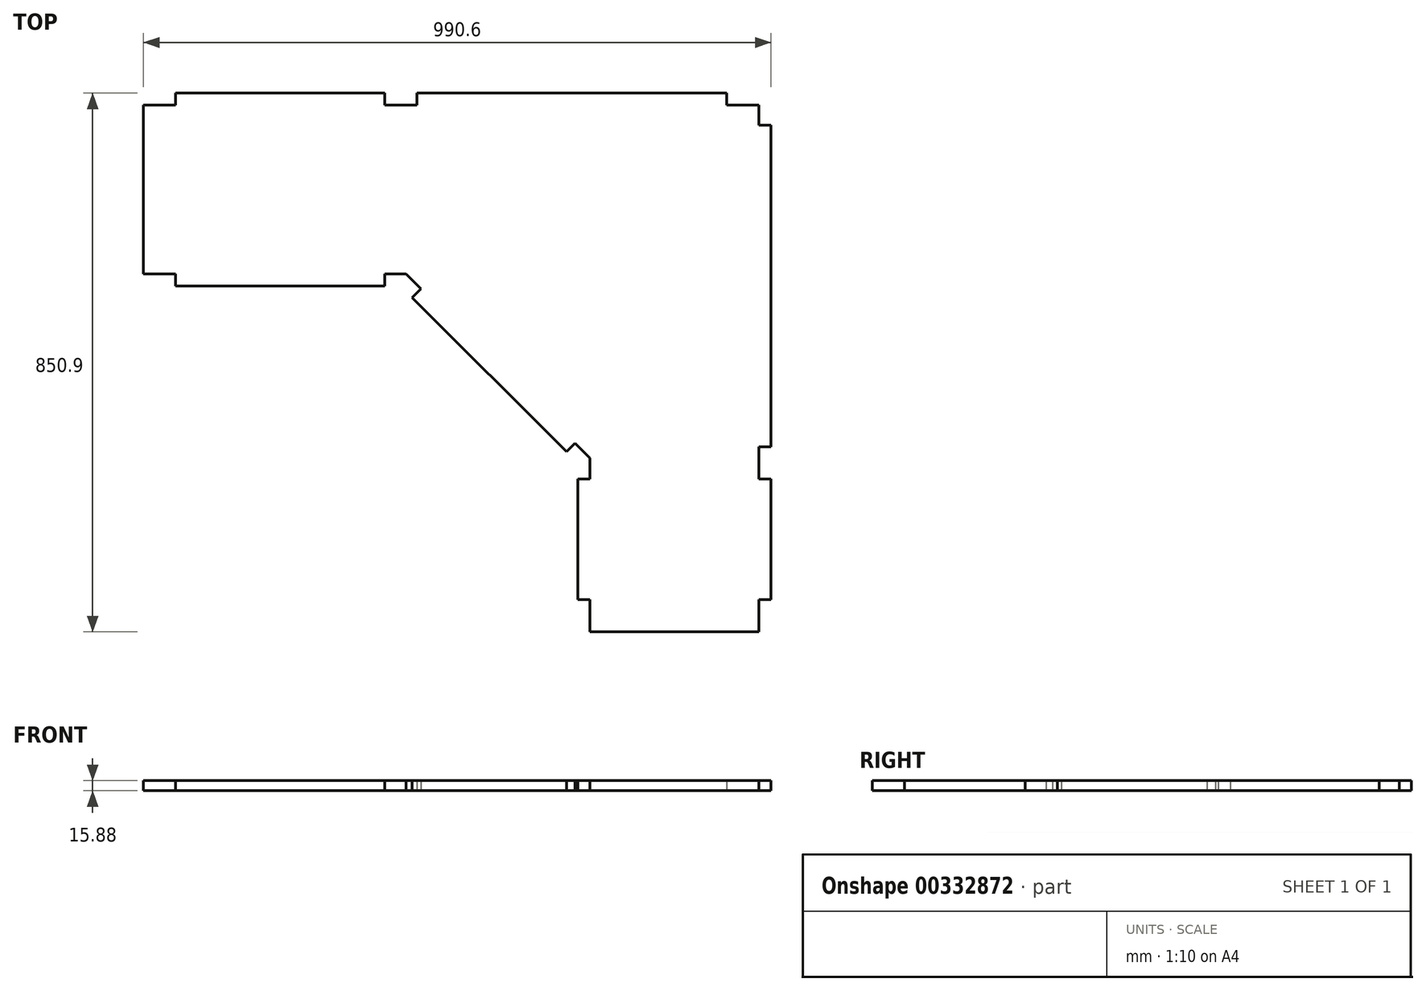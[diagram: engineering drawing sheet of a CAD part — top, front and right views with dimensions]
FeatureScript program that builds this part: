
annotation { "Feature Type Name" : "Feature", "Feature Type Description" : "" }
export const myFeature = defineFeature(function(context is Context, id is Id, definition is map)
    precondition{}
    {
        {
            var Q0;
            Q0=qCreatedBy(makeId("Top.planeOp"),FACE);
            var sketch = newSketch(context, id + "F0", { "sketchPlane" : qUnion([Q0])});
            skLineSegment(sketch, "E0.bottom", {"start": v(209.55, -425.45) * mm, "end": v(476.25, -425.45) * mm});
            skLineSegment(sketch, "E0.top", {"start": v(-444.5, 425.45) * mm, "end": v(-114.41, 425.45) * mm});
            skLineSegment(sketch, "E0.left", {"start": v(-495.3, 139.7) * mm, "end": v(-495.3, 406.4) * mm});
            skLineSegment(sketch, "E0.right", {"start": v(495.3, -374.65) * mm, "end": v(495.3, -184.26) * mm});
            skPoint(sketch, "E0.middle", {"position": v(0, 0) * mm});
            skLineSegment(sketch, "E1.left", {"start": v(190.5, -374.65) * mm, "end": v(190.5, -184.26) * mm});
            skPoint(sketch, "E2.orphan", {"position": v(-495.3, -425.45) * mm});
            skLineSegment(sketch, "E3", {"start": v(172.54, -140.9) * mm, "end": v(-71.05, 102.69) * mm});
            skLineSegment(sketch, "E4", {"start": v(-444.5, 120.65) * mm, "end": v(-114.41, 120.65) * mm});
            skLineSegment(sketch, "E5.top", {"start": v(-495.3, 139.7) * mm, "end": v(-444.5, 139.7) * mm});
            skLineSegment(sketch, "E5.right", {"start": v(-444.5, 120.65) * mm, "end": v(-444.5, 139.7) * mm});
            skLineSegment(sketch, "E6.top", {"start": v(-495.3, 406.4) * mm, "end": v(-444.5, 406.4) * mm});
            skLineSegment(sketch, "E6.right", {"start": v(-444.5, 425.45) * mm, "end": v(-444.5, 406.4) * mm});
            skLineSegment(sketch, "E7.top", {"start": v(190.5, -374.65) * mm, "end": v(209.55, -374.65) * mm});
            skLineSegment(sketch, "E7.right", {"start": v(209.55, -425.45) * mm, "end": v(209.55, -374.65) * mm});
            skLineSegment(sketch, "E8.top", {"start": v(476.25, -374.65) * mm, "end": v(495.3, -374.65) * mm});
            skLineSegment(sketch, "E8.left", {"start": v(476.25, -425.45) * mm, "end": v(476.25, -374.65) * mm});
            skPoint(sketch, "E9.orphan", {"position": v(-495.3, 425.45) * mm});
            skPoint(sketch, "E10.orphan", {"position": v(495.3, -425.45) * mm});
            skLineSegment(sketch, "E11.top", {"start": v(476.25, 406.4) * mm, "end": v(425.45, 406.4) * mm});
            skLineSegment(sketch, "E11.right", {"start": v(425.45, 425.45) * mm, "end": v(425.45, 406.4) * mm});
            skLineSegment(sketch, "E12.bottom", {"start": v(476.25, 374.65) * mm, "end": v(495.3, 374.65) * mm});
            skLineSegment(sketch, "E12.left", {"start": v(476.25, 374.65) * mm, "end": v(476.25, 406.4) * mm});
            skPoint(sketch, "E13.orphan", {"position": v(495.3, 425.45) * mm});
            skLineSegment(sketch, "E14.top", {"start": v(-114.41, 139.7) * mm, "end": v(-81.12, 139.7) * mm});
            skLineSegment(sketch, "E14.left", {"start": v(-114.41, 120.65) * mm, "end": v(-114.41, 139.7) * mm});
            skLineSegment(sketch, "E15.bottom", {"start": v(190.5, -184.26) * mm, "end": v(209.55, -184.26) * mm});
            skLineSegment(sketch, "E15.right", {"start": v(209.55, -184.26) * mm, "end": v(209.55, -150.97) * mm});
            skLineSegment(sketch, "E16", {"start": v(-81.12, 139.7) * mm, "end": v(-57.58, 116.16) * mm});
            skLineSegment(sketch, "E17", {"start": v(172.54, -140.9) * mm, "end": v(186, -127.43) * mm});
            skPoint(sketch, "E18.orphan", {"position": v(190.5, -158.86) * mm});
            skLineSegment(sketch, "E19", {"start": v(-71.05, 102.69) * mm, "end": v(-57.58, 116.16) * mm});
            skPoint(sketch, "E20.orphan", {"position": v(-89.01, 120.65) * mm});
            skLineSegment(sketch, "E21.trimOffspring", {"start": v(186, -127.43) * mm, "end": v(209.55, -150.97) * mm});
            skLineSegment(sketch, "E22.bottom", {"start": v(-114.41, 406.4) * mm, "end": v(-63.61, 406.4) * mm});
            skLineSegment(sketch, "E22.left", {"start": v(-114.41, 406.4) * mm, "end": v(-114.41, 425.45) * mm});
            skLineSegment(sketch, "E22.right", {"start": v(-63.61, 406.4) * mm, "end": v(-63.61, 425.45) * mm});
            skLineSegment(sketch, "E23.bottom", {"start": v(476.25, -184.26) * mm, "end": v(495.3, -184.26) * mm});
            skLineSegment(sketch, "E23.top", {"start": v(476.25, -133.46) * mm, "end": v(495.3, -133.46) * mm});
            skLineSegment(sketch, "E23.left", {"start": v(476.25, -184.26) * mm, "end": v(476.25, -133.46) * mm});
            skLineSegment(sketch, "E24.trimOffspring", {"start": v(-63.61, 425.45) * mm, "end": v(425.45, 425.45) * mm});
            skLineSegment(sketch, "E25.trimOffspring", {"start": v(495.3, -133.46) * mm, "end": v(495.3, 374.65) * mm});
            skSolve(sketch);
        }
        {
            var Q0;
            Q0=qSketchRegion(id+"F0",true);
            extrude(context, id + "F1", {"entities" : qUnion([Q0]), "depth" : 15.88 * mm});
        }
    });
